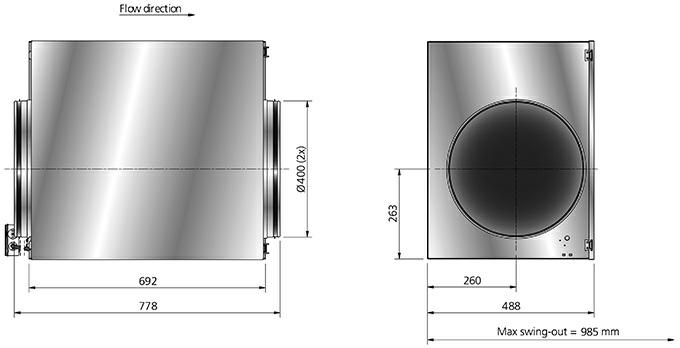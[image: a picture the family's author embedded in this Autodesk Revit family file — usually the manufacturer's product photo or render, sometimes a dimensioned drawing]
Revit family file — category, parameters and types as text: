
# Revit family: IRE 500 C3 ErP AC_7900040
name_source: partatom
category: Mechanical Equipment
revit_build: Autodesk Revit MEP 2014 (Build: 20130308_1515(x64)
units: mm (PartAtom-declared; Revit-internal decimal feet)

## types (1)
- IRE 500 C3 ErP AC
    Capacitor = - μF
    Current = 3 A
    Depth = 780 mm  [stored 2.55906 ft]
    Description = Insulated duct fans with circular connections
    Diameter = 500 mm  [stored 1.64042 ft]
    Frequency = 50 Hz
    Height = 584 mm  [stored 1.91601 ft]
    Main Material = Steel, Galvanized
    Max. temperature of transported air = 55 °C
    Max. temperature of transported air when speed controlled = 55 °C
    Phase = 3
    Power = 1300 W
    Sound pressure level at 3 m = 44 dB(A)
    Speed = 800 rpm
    Voltage = 400 V
    Voltage range = 380-415 V
    Weight = 71.30 kg
    Width = 907 mm  [stored 2.97572 ft]
    Wiring diagram = Y 4040004 / Δ 4040003

note: [stored X ft] marks values corroborated as IEEE doubles in the binary element streams (Revit-internal decimal feet)

## geometry (parser evidence)
native form markers: Sweep x5
no freeform markers — native parametric forms only
